# Revit family: SystemSchroeders_1flg.Tür
name_source: partatom
category: Türen
revit_build: Autodesk Revit 2018 (Build: 20170223_1515(x64)
units: mm (PartAtom-declared; Revit-internal decimal feet)

## family parameters
Basisbauteil = Wand
Beim Laden mit Abzugskörper schneiden = Nein
Gemeinsam genutzt = Nein
Immer vertikal = Ja
OmniClass-Nummer = 23.30.10.00
OmniClass-Titel = Doors
Raumberechnungspunkt = Nein

## types (12) — shared parameters
Analytische Konstruktion = <None>
Breite Rahmen Sichtfenster = 55 mm
Breite Sichtfenster = 260 mm  [stored 0.853018 ft]
Dicke = 69 mm  [stored 0.226378 ft]
Einbauhöhe Sichtfenster = 1500 mm
FrameCompensate = Edelstahl
Funktion = Innen
Hbl = 260 mm  [stored 0.853018 ft]
Hersteller = System Schröders
Höhe = 2200 mm
Höhe Sichtfenster = 260 mm  [stored 0.853018 ft]
Höhe Türgriff = 1050 mm
Luftdichtigkeit = bis Klasse 4 (600 Pa)
Rahmenbreite = 22 mm
URL = https://www.system-schroeders.de
Wandabschluss = Nach Basisbauteil
Werkstoff Griff = Edelstahl
Werkstoff Rahmen = Edelstahl
Werkstoff Rahmen Sichtfenster = Edelstahl
Werkstoff Sichtfenster = Glas
Werkstoff Türblatt = Edelstahl
Widerstandsfähigkeit gegen Winlast = bis Klasse C5 (2.000 Pa)
Öffnungswinkel = 90.00°

## per-type parameters (varying)
| type | Breite | Druck- / Sogwiderstand | Einbruchschutz | Feuerschutz | PanelWidth | Rauchschutz | Schallschutz | Schlagregendichtheit |
| ESN-1 | 1200 mm | 5000Pa | RC4 RC3 RC2 RC1 | - | 1157 mm  [stored 3.79593 ft] | - | 53 (-1;-5) dB | bis Klasse 8A |
| SN-1 | 1100 mm | 5000Pa | - | - | 1057 mm | - | 53 (-1;-5) dB | bis Klasse 8A |
| EIS-11 | 1200 mm | 5000Pa | - | EI2 120 -S a -C5 | 1157 mm  [stored 3.79593 ft] | S200 | - | bis Klasse 8A |
| TSN-3 CE | 1200 mm | 5000Pa | RC4 RC3 RC2 RC1 | EI2 60 -S a -C5 | 1157 mm  [stored 3.79593 ft] | S200 | 53 (-1;-5) dB | bis Klasse 8A |
| ASN-1 | 1200 mm | 5000Pa | - | - | 1157 mm  [stored 3.79593 ft] | - | - | bis Klasse 8A |
| TSN-1 CE | 1200 mm | 5000Pa | RC4 RC3 RC2 RC1 | EI2 30 -S a -C5 | 1157 mm  [stored 3.79593 ft] | S200 | 53 (-1;-5) dB | bis Klasse 8A |
| ISN-1 | 1200 mm | - | - | - | 1157 mm  [stored 3.79593 ft] | - | - | bis Klasse 8A |
| TSN-11 CE | 1200 mm | 5000Pa | RC4 RC3 RC2 RC1 | EI2 90 -S a -C5 | 1157 mm  [stored 3.79593 ft] | S200 | 53 (-1;-5) dB | bis Klasse 8A |
| RSN-1 | 1200 mm | 5000Pa | RC4 RC3 RC2 RC1 | - | 1157 mm  [stored 3.79593 ft] | RS | 53 (-1;-5) dB | bis Klasse 8A |
| TSN-11 | 1200 mm | 5000Pa | RC4 RC3 RC2 RC1 | T-90 | 1157 mm  [stored 3.79593 ft] | RS | 53 (-1;-5) dB |  |
| TSN-1 | 1200 mm | 5000Pa | RC4 RC3 RC2 RC1 | T-30 | 1157 mm  [stored 3.79593 ft] | RS | 53 (-1;-5) dB |  |
| RSN-1 CE | 1200 mm | 5000Pa | RC4 RC3 RC2 RC1 | - | 1157 mm  [stored 3.79593 ft] | RS | 53 (-1;-5) dB | bis Klasse 8A |

note: [stored X ft] marks values corroborated as IEEE doubles in the binary element streams (Revit-internal decimal feet)

## geometry (parser evidence)
native form markers: Sweep x4
no freeform markers — native parametric forms only
